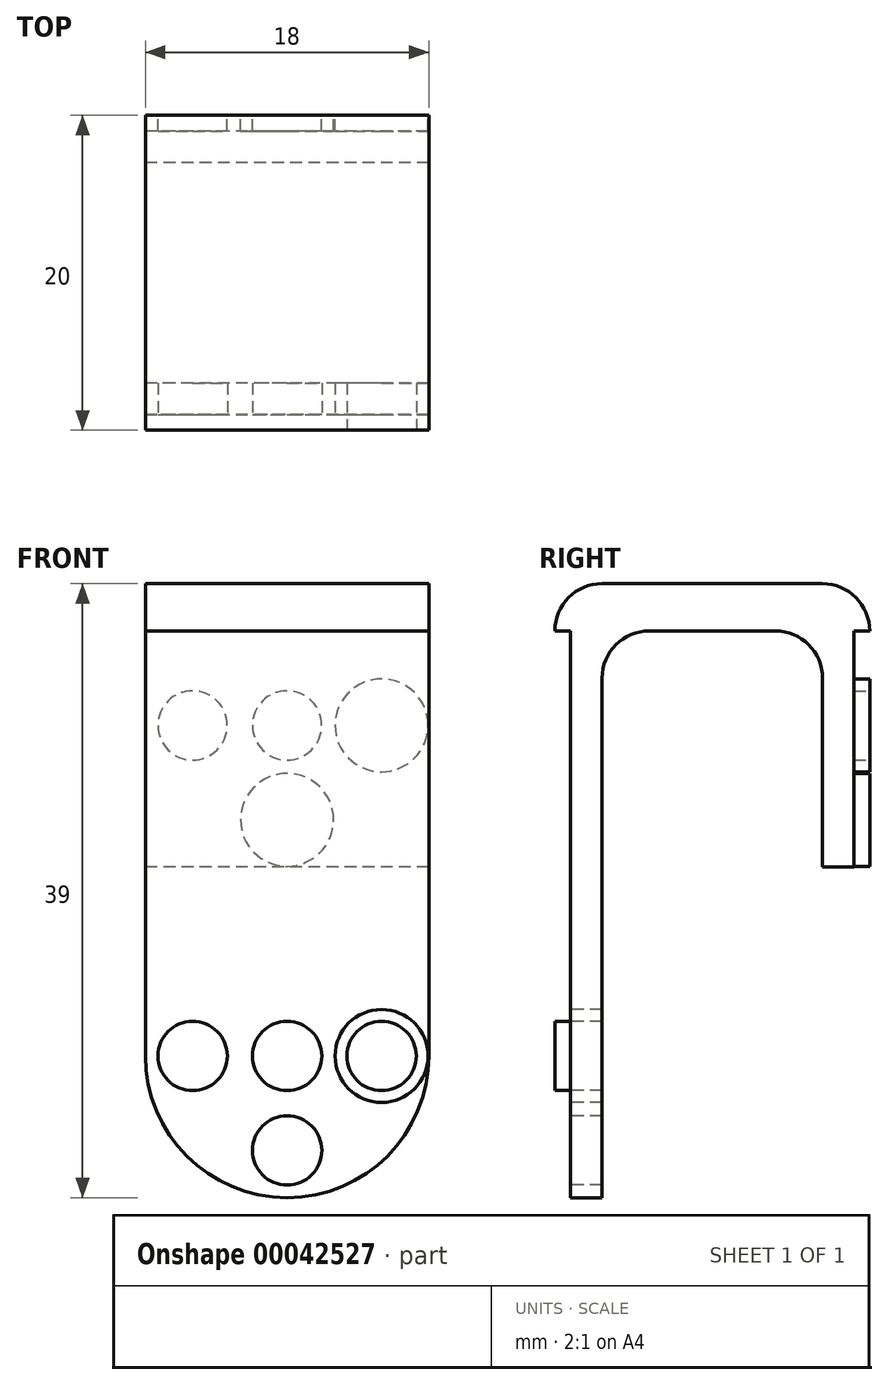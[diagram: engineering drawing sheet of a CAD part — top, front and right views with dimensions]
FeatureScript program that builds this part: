
annotation { "Feature Type Name" : "Feature", "Feature Type Description" : "" }
export const myFeature = defineFeature(function(context is Context, id is Id, definition is map)
    precondition{}
    {
        {
            var Q0;
            Q0=qCreatedBy(makeId("Right.planeOp"),FACE);
            var sketch = newSketch(context, id + "F0", { "sketchPlane" : qUnion([Q0])});
            skLineSegment(sketch, "E0", {"start": v(10, 15) * mm, "end": v(10, 0) * mm});
            skLineSegment(sketch, "E1", {"start": v(-7, 18) * mm, "end": v(7, 18) * mm});
            skLineSegment(sketch, "E2.0", {"start": v(7, 15) * mm, "end": v(7, 0) * mm});
            skLineSegment(sketch, "E2.1", {"start": v(-7, 15) * mm, "end": v(7, 15) * mm});
            skLineSegment(sketch, "E3", {"start": v(7, 0) * mm, "end": v(10, 0) * mm});
            skPoint(sketch, "E4.visualSharp", {"position": v(-10, 18) * mm});
            skArc(sketch, "E4.filletArc", {"start": v(-7, 18) * mm, "mid": v(-9.12, 17.12) * mm, "end": v(-10, 15) * mm});
            skPoint(sketch, "E5.visualSharp", {"position": v(10, 18) * mm});
            skArc(sketch, "E5.filletArc", {"start": v(10, 15) * mm, "mid": v(9.12, 17.12) * mm, "end": v(7, 18) * mm});
            skPoint(sketch, "E6.start.orphan", {"position": v(-10, 0) * mm});
            skLineSegment(sketch, "E7", {"start": v(-7, 15) * mm, "end": v(-7, -21) * mm});
            skLineSegment(sketch, "E8", {"start": v(-10, 15) * mm, "end": v(-10, -21) * mm});
            skLineSegment(sketch, "E9", {"start": v(-7, -21) * mm, "end": v(-10, -21) * mm});
            skSolve(sketch);
        }
        {
            var Q0;
            Q0=makeQuery(id+"F0.imprint","IMPRINT",FACE,{"disambiguationData":[TD([[makeQuery(id+"F0.imprint","IMPRINT",EDGE,{"derivedFrom":sQuery(id+"F0.wireOp",EDGE,"E0")}),-1.0]])]});
            extrude(context, id + "F1", {"entities" : qUnion([Q0]), "depth" : 18 * mm});
        }
        {
            var Q0;
            Q0=makeQuery(id+"F1.opExtrude","SWEPT_FACE",FACE,{"disambiguationData":[OSD([sQuery(id+"F0.wireOp",EDGE,"E0")])]});
            var sketch = newSketch(context, id + "F2", { "sketchPlane" : qUnion([Q0])});
            skPoint(sketch, "E10", {"position": v(-18, 19.15) * mm});
            skPoint(sketch, "E11", {"position": v(-18, 1.15) * mm});
            skPoint(sketch, "E12", {"position": v(0, 1.15) * mm});
            skPoint(sketch, "E13", {"position": v(0, 19.15) * mm});
            skPoint(sketch, "E14", {"position": v(-9, 9) * mm});
            skCircle(sketch, "E15", {"center": v(-3, 9) * mm, "radius": 2.95 * mm});
            skCircle(sketch, "E16", {"center": v(-9, 9) * mm, "radius": 2.2 * mm});
            skCircle(sketch, "E17", {"center": v(-9, 9) * mm, "radius": 2.95 * mm});
            skCircle(sketch, "E18", {"center": v(-3, 9) * mm, "radius": 2.2 * mm});
            skLineSegment(sketch, "E19", {"start": v(-9, 1.15) * mm, "end": v(-9, 19.15) * mm, "construction": true});
            skLineSegment(sketch, "E20", {"start": v(-18, 9) * mm, "end": v(0, 9) * mm, "construction": true});
            skCircle(sketch, "E21.MirrorC", {"center": v(-9, 3) * mm, "radius": 2.95 * mm});
            skCircle(sketch, "E22.MirrorC", {"center": v(-9, 3) * mm, "radius": 2.2 * mm});
            skCircle(sketch, "E23.MirrorC", {"center": v(-15, 9) * mm, "radius": 2.95 * mm});
            skCircle(sketch, "E24.MirrorC", {"center": v(-15, 9) * mm, "radius": 2.2 * mm});
            skSolve(sketch);
        }
        {
            var Q0;
            Q0=makeQuery(id+"F2.imprint","IMPRINT",FACE,{"disambiguationData":[TD([[makeQuery(id+"F2.imprint","IMPRINT",EDGE,{"derivedFrom":sQuery(id+"F2.wireOp",EDGE,"E23.MirrorC")}),-1.0]])]});
            var Q1;
            Q1=makeQuery(id+"F2.imprint","IMPRINT",FACE,{"disambiguationData":[TD([[makeQuery(id+"F2.imprint","IMPRINT",EDGE,{"derivedFrom":sQuery(id+"F2.wireOp",EDGE,"E17")}),1.0]])]});
            var Q2;
            Q2=makeQuery(id+"F2.imprint","IMPRINT",FACE,{"disambiguationData":[TD([[makeQuery(id+"F2.imprint","IMPRINT",EDGE,{"derivedFrom":sQuery(id+"F2.wireOp",EDGE,"E15")}),1.0]])]});
            var Q3;
            Q3=makeQuery(id+"F2.imprint","IMPRINT",FACE,{"disambiguationData":[TD([[makeQuery(id+"F2.imprint","IMPRINT",EDGE,{"derivedFrom":sQuery(id+"F2.wireOp",EDGE,"E21.MirrorC")}),-1.0]])]});
            extrude(context, id + "F3", {"entities" : qUnion([Q0, Q1, Q2, Q3]), "operationType" : NewBodyOperationType.REMOVE, "oppositeDirection" : true, "depth" : 1 * mm});
        }
        {
            var Q0;
            Q0=makeQuery(id+"F1.opExtrude","SWEPT_EDGE",EDGE,{"disambiguationData":[OSD([sQuery(id+"F0.wireOp",EDGE,"E2.1"),sQuery(id+"F0.wireOp",EDGE,"E2.2")])]});
            var Q1;
            Q1=makeQuery(id+"F1.opExtrude","SWEPT_EDGE",EDGE,{"disambiguationData":[OSD([sQuery(id+"F0.wireOp",EDGE,"E2.0"),sQuery(id+"F0.wireOp",EDGE,"E2.1")])]});
            fillet(context, id + "F4", {"entities" : qUnion([Q0, Q1]), "radius" : 3 * mm, "tangentPropagation" : true, "allowEdgeOverflow" : false});
        }
        {
            var Q0;
            Q0=makeQuery(id+"F1.opExtrude","SWEPT_FACE",FACE,{"disambiguationData":[OSD([sQuery(id+"F0.wireOp",EDGE,"E8")])]});
            var sketch = newSketch(context, id + "F5", { "sketchPlane" : qUnion([Q0])});
            skLineSegment(sketch, "E25", {"start": v(9, -21) * mm, "end": v(9, 15) * mm, "construction": true});
            skCircle(sketch, "E26", {"center": v(9, -18) * mm, "radius": 2.95 * mm});
            skCircle(sketch, "E27", {"center": v(9, -18) * mm, "radius": 2.2 * mm});
            skCircle(sketch, "E28", {"center": v(9, -12) * mm, "radius": 2.95 * mm});
            skCircle(sketch, "E29", {"center": v(9, -12) * mm, "radius": 2.2 * mm});
            skLineSegment(sketch, "E30", {"start": v(9, -12) * mm, "end": v(0, -12) * mm, "construction": true});
            skCircle(sketch, "E31", {"center": v(3, -12) * mm, "radius": 2.95 * mm});
            skCircle(sketch, "E32", {"center": v(3, -12) * mm, "radius": 2.2 * mm});
            skCircle(sketch, "E33.MirrorC", {"center": v(15, -12) * mm, "radius": 2.95 * mm});
            skCircle(sketch, "E34.MirrorC", {"center": v(15, -12) * mm, "radius": 2.2 * mm});
            skArc(sketch, "E35", {"start": v(0, -12) * mm, "mid": v(9, -21) * mm, "end": v(18, -12) * mm});
            skSolve(sketch);
        }
        {
            var Q0;
            {var subQ0=sQuery(id+"F5.wireOp",EDGE,"E35");var subQ1=sQuery(id+"F0.wireOp",EDGE,"E8");var subQ2=makeQuery(id+"F1.opExtrude","CAP_EDGE",EDGE,{"disambiguationData":[OSD([subQ1])],"isStart":false});var subQ3=makeQuery(id+"F5.imprint","INTERSECT",VERTEX,{"derivedFrom":[subQ2,subQ0]});Q0=makeQuery(id+"F5.imprint","IMPRINT",FACE,{"disambiguationData":[TD([[makeQuery(id+"F5.imprint","IMPRINT",EDGE,{"disambiguationData":[TD([[subQ3,1.0]])],"derivedFrom":subQ0}),-1.0]])]});}
            var Q1;
            {var subQ0=sQuery(id+"F5.wireOp",EDGE,"E35");var subQ1=sQuery(id+"F0.wireOp",EDGE,"E8");var subQ2=makeQuery(id+"F1.opExtrude","CAP_EDGE",EDGE,{"disambiguationData":[OSD([subQ1])],"isStart":true});var subQ3=makeQuery(id+"F5.imprint","INTERSECT",VERTEX,{"derivedFrom":[subQ2,subQ0]});Q1=makeQuery(id+"F5.imprint","IMPRINT",FACE,{"disambiguationData":[TD([[makeQuery(id+"F5.imprint","IMPRINT",EDGE,{"disambiguationData":[TD([[subQ3,-1.0]])],"derivedFrom":subQ0}),-1.0]])]});}
            var Q2;
            Q2=makeQuery(id+"F5.imprint","IMPRINT",FACE,{"disambiguationData":[TD([[makeQuery(id+"F5.imprint","IMPRINT",EDGE,{"derivedFrom":sQuery(id+"F5.wireOp",EDGE,"E32")}),1.0]])]});
            var Q3;
            Q3=makeQuery(id+"F5.imprint","IMPRINT",FACE,{"disambiguationData":[TD([[makeQuery(id+"F5.imprint","IMPRINT",EDGE,{"derivedFrom":sQuery(id+"F5.wireOp",EDGE,"E29")}),1.0]])]});
            var Q4;
            Q4=makeQuery(id+"F5.imprint","IMPRINT",FACE,{"disambiguationData":[TD([[makeQuery(id+"F5.imprint","IMPRINT",EDGE,{"derivedFrom":sQuery(id+"F5.wireOp",EDGE,"E34.MirrorC")}),-1.0]])]});
            var Q5;
            Q5=makeQuery(id+"F5.imprint","IMPRINT",FACE,{"disambiguationData":[TD([[makeQuery(id+"F5.imprint","IMPRINT",EDGE,{"derivedFrom":sQuery(id+"F5.wireOp",EDGE,"E27")}),1.0]])]});
            extrude(context, id + "F6", {"entities" : qUnion([Q0, Q1, Q2, Q3, Q4, Q5]), "operationType" : NewBodyOperationType.REMOVE, "endBound" : BoundingType.THROUGH_ALL, "oppositeDirection" : true, "depth" : 25 * mm});
        }
        {
            var Q0;
            Q0=makeQuery(id+"F5.imprint","IMPRINT",FACE,{"disambiguationData":[TD([[makeQuery(id+"F5.imprint","IMPRINT",EDGE,{"derivedFrom":sQuery(id+"F5.wireOp",EDGE,"E31")}),1.0]])]});
            var Q1;
            Q1=makeQuery(id+"F5.imprint","IMPRINT",FACE,{"disambiguationData":[TD([[makeQuery(id+"F5.imprint","IMPRINT",EDGE,{"derivedFrom":sQuery(id+"F5.wireOp",EDGE,"E28")}),1.0]])]});
            var Q2;
            Q2=makeQuery(id+"F5.imprint","IMPRINT",FACE,{"disambiguationData":[TD([[makeQuery(id+"F5.imprint","IMPRINT",EDGE,{"derivedFrom":sQuery(id+"F5.wireOp",EDGE,"E33.MirrorC")}),-1.0]])]});
            var Q3;
            Q3=makeQuery(id+"F5.imprint","IMPRINT",FACE,{"disambiguationData":[TD([[makeQuery(id+"F5.imprint","IMPRINT",EDGE,{"derivedFrom":sQuery(id+"F5.wireOp",EDGE,"E26")}),1.0]])]});
            extrude(context, id + "F7", {"entities" : qUnion([Q0, Q1, Q2, Q3]), "operationType" : NewBodyOperationType.REMOVE, "oppositeDirection" : true, "depth" : 1 * mm});
        }
    });
